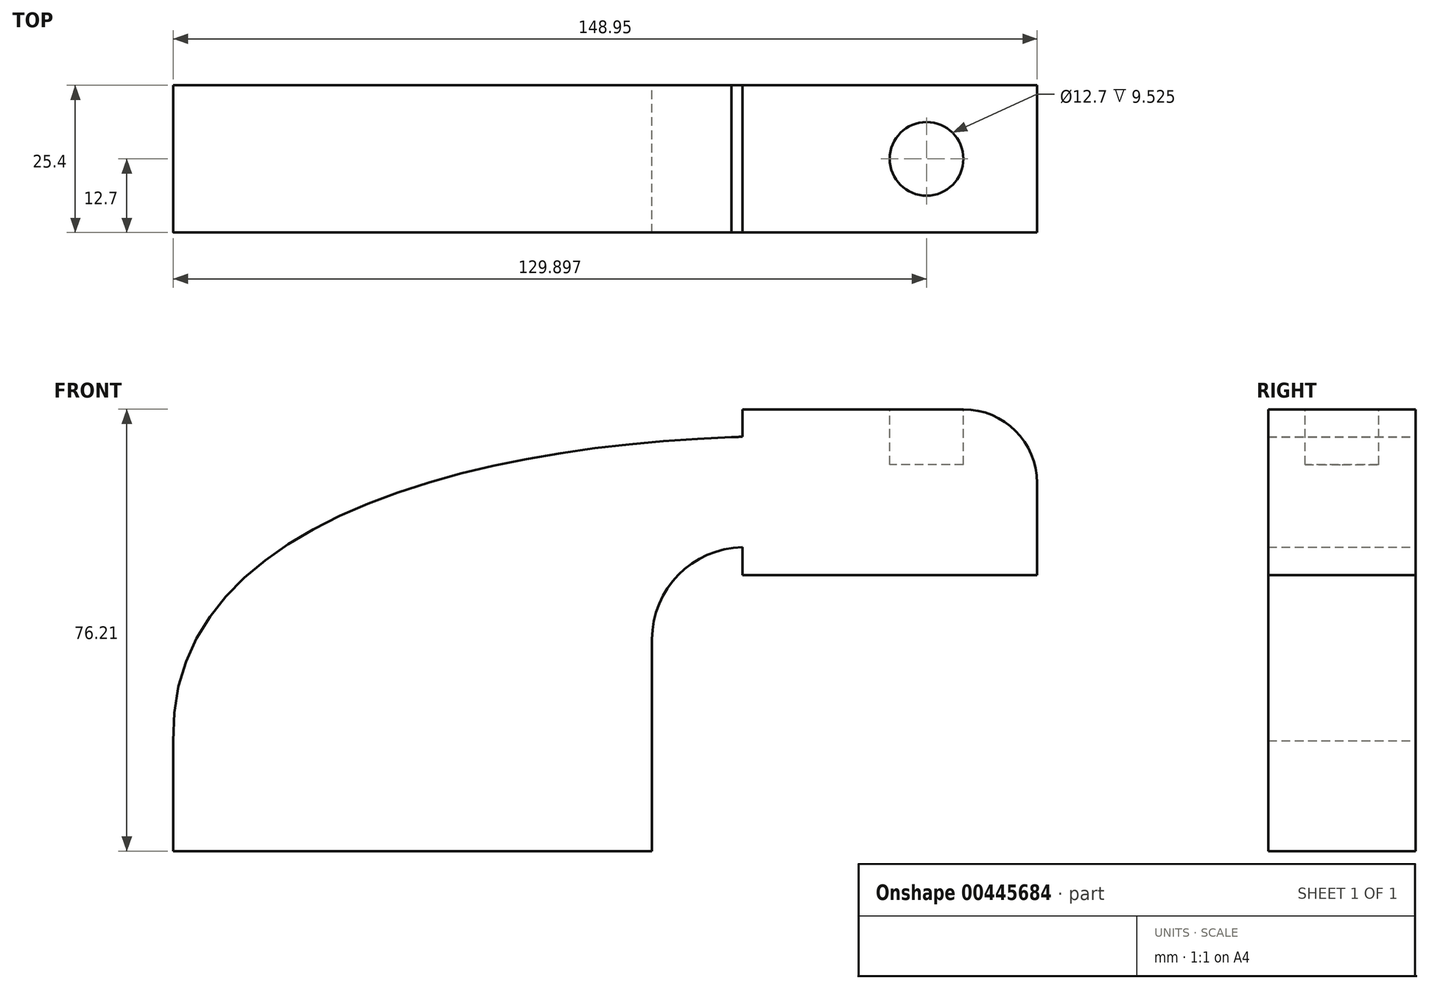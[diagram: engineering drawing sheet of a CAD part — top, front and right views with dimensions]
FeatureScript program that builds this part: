
annotation { "Feature Type Name" : "Feature", "Feature Type Description" : "" }
export const myFeature = defineFeature(function(context is Context, id is Id, definition is map)
    precondition{}
    {
        {
            var Q0;
            Q0=qCreatedBy(makeId("Front.planeOp"),FACE);
            var sketch = newSketch(context, id + "F0", { "sketchPlane" : qUnion([Q0])});
            skLineSegment(sketch, "E0.bottom", {"start": v(-41.28, -9.53) * mm, "end": v(41.28, -9.53) * mm});
            skLineSegment(sketch, "E0.top", {"start": v(-41.28, 9.53) * mm, "end": v(41.28, 9.53) * mm});
            skLineSegment(sketch, "E0.left", {"start": v(-41.28, -9.53) * mm, "end": v(-41.28, 9.53) * mm});
            skLineSegment(sketch, "E0.right", {"start": v(41.28, -9.53) * mm, "end": v(41.28, 9.53) * mm});
            skPoint(sketch, "E0.middle", {"position": v(0, 0) * mm});
            skLineSegment(sketch, "E1.bottom", {"start": v(56.86, 38.1) * mm, "end": v(107.66, 38.1) * mm});
            skLineSegment(sketch, "E1.top", {"start": v(56.86, 66.67) * mm, "end": v(107.66, 66.67) * mm});
            skLineSegment(sketch, "E1.left", {"start": v(56.86, 38.1) * mm, "end": v(56.86, 66.67) * mm});
            skLineSegment(sketch, "E1.right", {"start": v(107.66, 38.1) * mm, "end": v(107.66, 66.67) * mm});
            skPoint(sketch, "E1.middle", {"position": v(82.26, 52.39) * mm});
            skLineSegment(sketch, "E2", {"start": v(41.28, 9.53) * mm, "end": v(41.28, 27) * mm});
            skArc(sketch, "E3", {"start": v(41.27, 27) * mm, "mid": v(45.92, 38.23) * mm, "end": v(57.15, 42.88) * mm});
            skLineSegment(sketch, "E4", {"start": v(57.15, 42.88) * mm, "end": v(82.2, 42.88) * mm});
            skLineSegment(sketch, "E5.0", {"start": v(57.15, 61.93) * mm, "end": v(82.2, 61.93) * mm});
            skArc(sketch, "E5.1", {"start": v(22.22, 27) * mm, "mid": v(32.45, 51.7) * mm, "end": v(57.15, 61.93) * mm});
            skLineSegment(sketch, "E5.2", {"start": v(22.22, 9.53) * mm, "end": v(22.22, 27) * mm});
            skLineSegment(sketch, "E6", {"start": v(82.26, 66.67) * mm, "end": v(82.2, 38.1) * mm});
            skFitSpline(sketch, "E7", {"points": [v(-41.28, 9.53) * mm, v(57.15, 61.93) * mm], "startDerivative": vector(-3.47, 116.02) * mm, "endDerivative": vector(134.05, 3.7) * mm});
            skSolve(sketch);
        }
        {
            var Q0;
            Q0 = qSketchRegion(id + "F0", true);
            extrude(context, id + "F1", {"entities" : qUnion([Q0]), "depth" : 25.4 * mm});
        }
        {
            var Q0;
            Q0=makeQuery(id+"F1.opExtrude","SWEPT_FACE",FACE,{"disambiguationData":[OSD([sQuery(id+"F0.wireOp",EDGE,"E1.top")])]});
            var sketch = newSketch(context, id + "F2", { "sketchPlane" : qUnion([Q0])});
            skCircle(sketch, "E8", {"center": v(88.6, -12.7) * mm, "radius": 6.35 * mm});
            skSolve(sketch);
        }
        {
            var Q0;
            Q0 = qSketchRegion(id + "F2", true);
            extrude(context, id + "F3", {"entities" : qUnion([Q0]), "operationType" : NewBodyOperationType.REMOVE, "oppositeDirection" : true, "depth" : 9.52 * mm});
        }
        {
            var Q0;
            Q0=makeQuery(id+"F1.opExtrude","SWEPT_EDGE",EDGE,{"disambiguationData":[OSD([sQuery(id+"F0.wireOp",EDGE,"E1.top"),sQuery(id+"F0.wireOp",EDGE,"E1.right")])]});
            fillet(context, id + "F4", {"entities" : qUnion([Q0]), "radius" : 12.7 * mm, "tangentPropagation" : true, "allowEdgeOverflow" : false});
        }
    });
